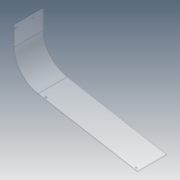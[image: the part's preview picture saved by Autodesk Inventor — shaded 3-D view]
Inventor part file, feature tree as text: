
AUTODESK INVENTOR PART (.ipt)
format: ipt  version: 2012 (Build 160160000, 160)  size: 91,136 bytes
history: native  units: in
note: dims shown in document units (in); Inventor stores cm internally (conversion verified against a paired STEP export)
features: hole x2, pattern_linear x2, extrude x1, sketch x1, reference x1
ambient origin geometry x8: Origin, YZ Plane, XZ Plane, XY Plane, X Axis, Y Axis, Z Axis, Center Point
bodies: Solid1 (feature_tree)
feature tree (7):
  extrude  "Extrusion1"  Depth=0.5in
  hole  "Hole1"  [1 undecoded]
  pattern_linear  "Rectangular Pattern1"  Spacing1=0.3125in  [1 undecoded]
  hole  "Hole2"  [1 undecoded]
  pattern_linear  "Rectangular Pattern2"  [2 undecoded]
  sketch  "Sketch1"  dims[d0=4.625in d1=0.0in d2=0.5in d3=0.3125in d4=0.265in d5=0.75in d6=0.375in d7=0.25in d8=0.5635in d9=1.0in d10=0.8108in d11=0.7874in d13=2.6875in d14=0.3125in d15=0.5in d16=0.265in d17=0.75in d18=0.375in d19=0.25in d20=0.5635in d21=1.0in d22=0.8108in d23=0.7874in d25=14.5in]
  reference  "Reference1"
note: 5 required parameter values undecoded (feature->parameter linkage not recoverable at this tier; creation-order binding heuristic only, values carry confidence <= 0.55)
